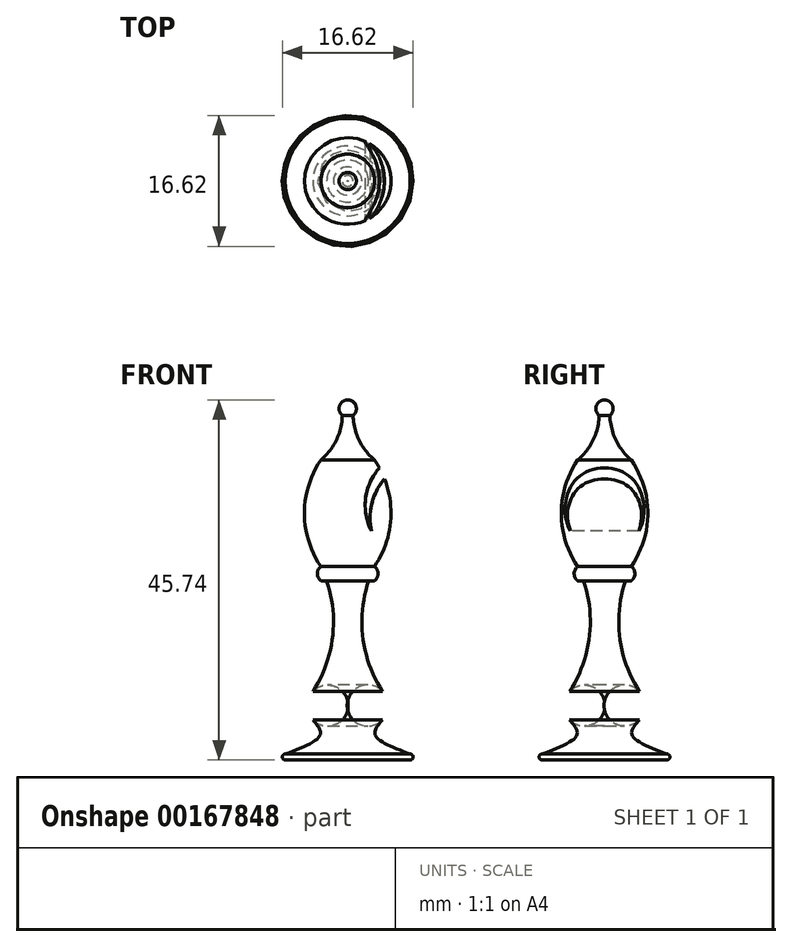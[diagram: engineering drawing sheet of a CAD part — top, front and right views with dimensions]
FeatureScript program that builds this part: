
annotation { "Feature Type Name" : "Feature", "Feature Type Description" : "" }
export const myFeature = defineFeature(function(context is Context, id is Id, definition is map)
    precondition{}
    {
        {
            var Q0;
            Q0=qCreatedBy(makeId("Front.planeOp"),FACE);
            var sketch = newSketch(context, id + "F0", { "sketchPlane" : qUnion([Q0])});
            skLineSegment(sketch, "E0", {"start": v(0, 38.1) * mm, "end": v(0, 0) * mm});
            skLineSegment(sketch, "E1", {"start": v(0, 0) * mm, "end": v(7.94, 0) * mm});
            skArc(sketch, "E2", {"start": v(2.67, 22.76) * mm, "mid": v(1.93, 15.54) * mm, "end": v(4.43, 8.71) * mm});
            skArc(sketch, "E3", {"start": v(4.43, 5.1) * mm, "mid": v(5.16, 6.9) * mm, "end": v(4.43, 8.71) * mm});
            skArc(sketch, "E4", {"start": v(3.4, 22.76) * mm, "mid": v(3.86, 23.67) * mm, "end": v(3.4, 24.58) * mm});
            skLineSegment(sketch, "E5", {"start": v(3.4, 22.76) * mm, "end": v(2.67, 22.76) * mm});
            skArc(sketch, "E6", {"start": v(7.94, 0) * mm, "mid": v(8.31, 0.38) * mm, "end": v(7.94, 0.75) * mm});
            skFitSpline(sketch, "E7", {"points": [v(4.43, 5.1) * mm, v(3.48, 3.2) * mm, v(7.94, 0.75) * mm], "startDerivative": vector(-4.32, -4.97) * mm, "endDerivative": vector(10.28, -3.8) * mm});
            skArc(sketch, "E8", {"start": v(3.4, 24.58) * mm, "mid": v(5.5, 31.34) * mm, "end": v(3.4, 38.1) * mm});
            skArc(sketch, "E9", {"start": v(0.69, 43.78) * mm, "mid": v(1.44, 40.65) * mm, "end": v(3.4, 38.1) * mm});
            skLineSegment(sketch, "E10", {"start": v(0, 38.1) * mm, "end": v(0, 47.8) * mm});
            skArc(sketch, "E11", {"start": v(0.69, 43.78) * mm, "mid": v(1.04, 45) * mm, "end": v(0, 45.74) * mm});
            skSolve(sketch);
        }
        {
            var Q0;
            Q0 = qSketchRegion(id + "F0", true);
            var Q1;
            Q1=sQuery(id+"F0.wireOp",EDGE,"E0");
            revolve(context, id + "F1", {"entities" : qUnion([Q0]), "axis" : qUnion([Q1]), "revolveType" : RevolveType.FULL});
        }
        {
            var Q0;
            Q0=qCreatedBy(makeId("Front.planeOp"),FACE);
            var sketch = newSketch(context, id + "F2", { "sketchPlane" : qUnion([Q0])});
            skArc(sketch, "E12.0", {"start": v(3.4, 24.58) * mm, "mid": v(5.5, 31.34) * mm, "end": v(3.4, 38.1) * mm});
            skArc(sketch, "E13.0", {"start": v(0.69, 43.78) * mm, "mid": v(1.44, 40.65) * mm, "end": v(3.4, 38.1) * mm});
            skArc(sketch, "E14.0", {"start": v(3.4, 22.76) * mm, "mid": v(3.86, 23.67) * mm, "end": v(3.4, 24.58) * mm});
            skArc(sketch, "E15", {"start": v(4.67, 35.71) * mm, "mid": v(3.07, 32.6) * mm, "end": v(3.02, 29.12) * mm});
            skArc(sketch, "E16", {"start": v(4.03, 37.1) * mm, "mid": v(2.27, 33.26) * mm, "end": v(3.02, 29.12) * mm});
            skSolve(sketch);
        }
        {
            var Q0;
            Q0 = qSketchRegion(id + "F2", true);
            extrude(context, id + "F3", {"entities" : qUnion([Q0]), "operationType" : NewBodyOperationType.REMOVE, "endBound" : BoundingType.SYMMETRIC, "oppositeDirection" : true, "depth" : 25.4 * mm});
        }
    });
